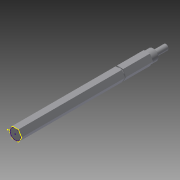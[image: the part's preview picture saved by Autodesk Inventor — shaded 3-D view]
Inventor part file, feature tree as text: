
AUTODESK INVENTOR PART (.ipt)
format: ipt  version: 2014 SP1 (Build 180222100, 222)  size: 126,976 bytes
history: native  units: in
note: dims shown in document units (in); Inventor stores cm internally (conversion verified against a paired STEP export)
features: sketch x3, imported_body x2, extrude x2, other x1
ambient origin geometry x8: Origin, YZ Plane, XZ Plane, XY Plane, X Axis, Y Axis, Z Axis, Center Point
bodies: Body1 (feature_tree)
feature tree (8):
  imported_body  "Imported1"
  other  "SS Wheel Shaft.ipt1"
  extrude  "Extrusion1"  Depth=4.259in TaperAngle=0.0deg
  sketch  "Sketch2"
  sketch  "Sketch3"
  extrude  "Extrusion2"  [1 undecoded]
  imported_body  "Base1"
  sketch  "Sketch1"  dims[d0=4.259in d1=0.0in d2=4.259in d3=0.0in]
note: 1 required parameter value undecoded (feature->parameter linkage not recoverable at this tier; creation-order binding heuristic only, values carry confidence <= 0.55)
